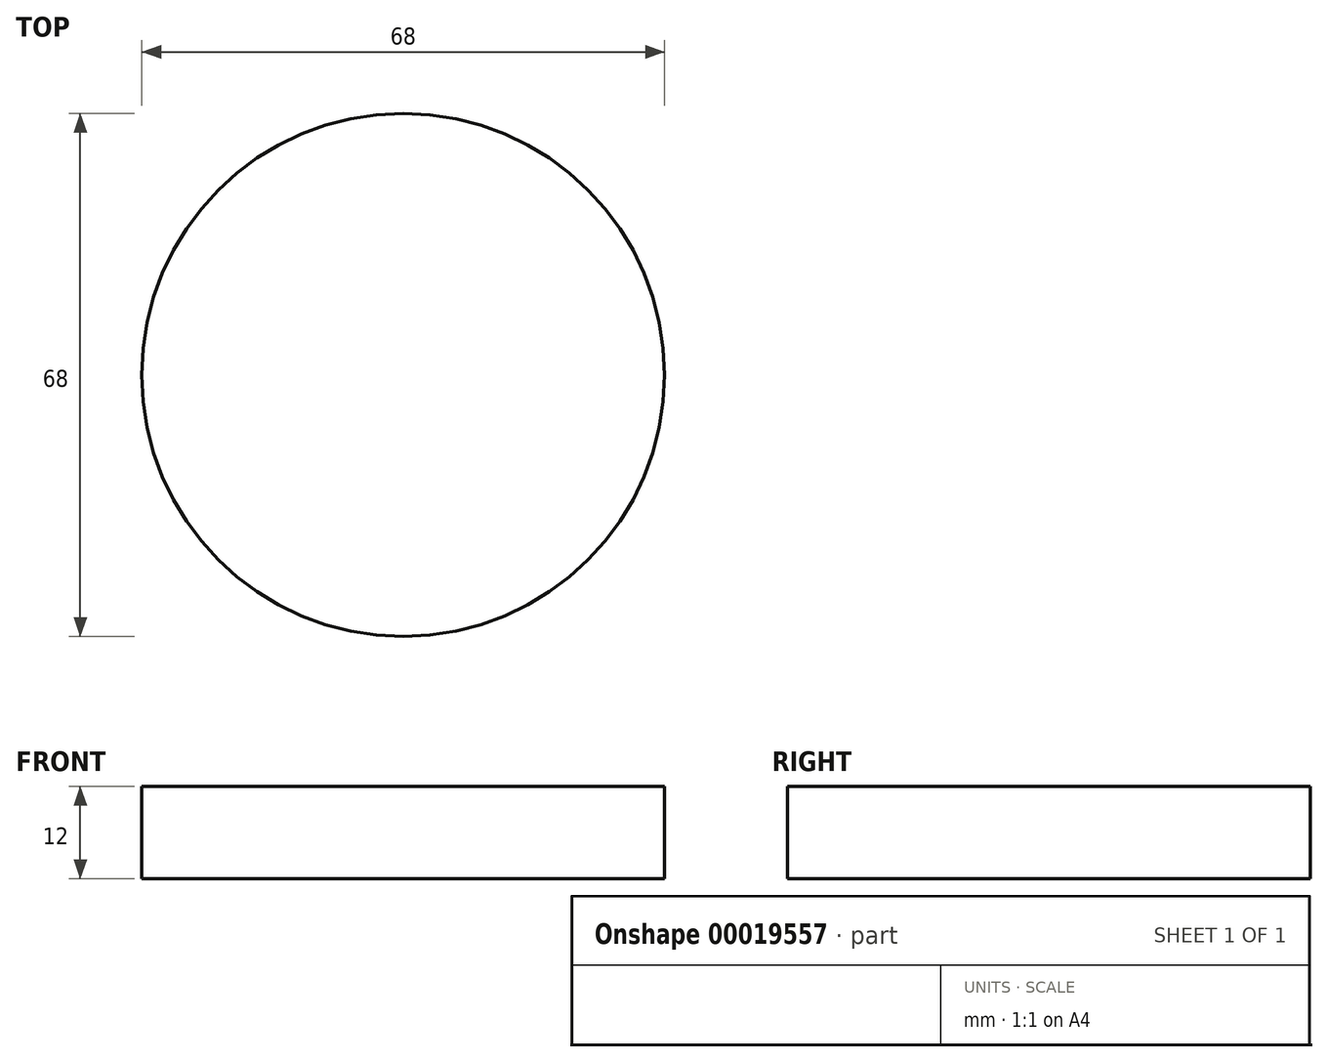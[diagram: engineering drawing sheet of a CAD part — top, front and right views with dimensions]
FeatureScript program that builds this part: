
annotation { "Feature Type Name" : "Feature", "Feature Type Description" : "" }
export const myFeature = defineFeature(function(context is Context, id is Id, definition is map)
    precondition{}
    {
        {
            var Q0;
            Q0=qCreatedBy(makeId("Top.planeOp"),FACE);
            var sketch = newSketch(context, id + "F0", { "sketchPlane" : qUnion([Q0])});
            skCircle(sketch, "E0", {"center": v(0, 0) * mm, "radius": 34 * mm});
            skSolve(sketch);
        }
        {
            var Q0;
            Q0 = qSketchRegion(id + "F0", true);
            extrude(context, id + "F1", {"entities" : qUnion([Q0]), "depth" : 12 * mm});
        }
    });
